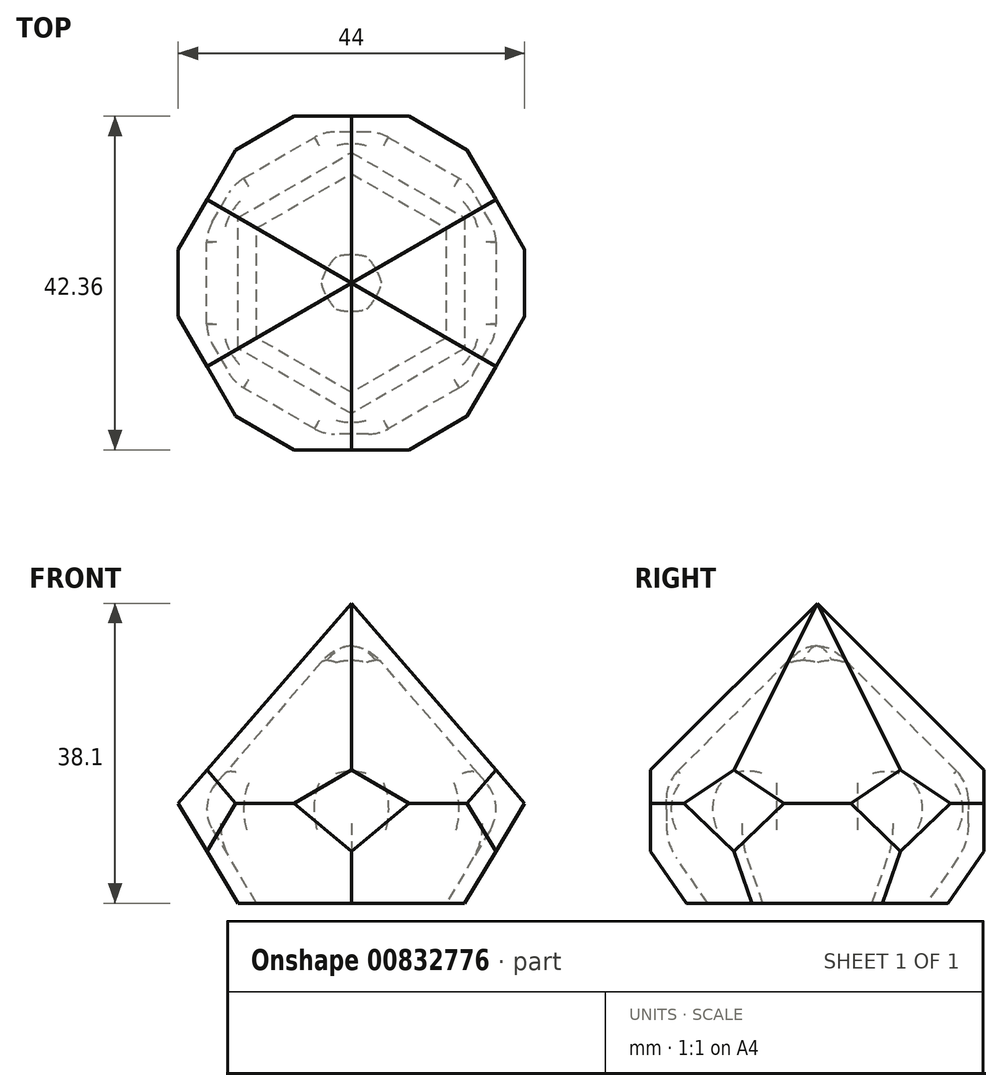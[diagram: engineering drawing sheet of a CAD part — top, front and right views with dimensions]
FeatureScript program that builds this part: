
annotation { "Feature Type Name" : "Feature", "Feature Type Description" : "" }
export const myFeature = defineFeature(function(context is Context, id is Id, definition is map)
    precondition{}
    {
        {
            var Q0;
            Q0=qCreatedBy(makeId("Top.planeOp"),FACE);
            var sketch = newSketch(context, id + "F0", { "sketchPlane" : qUnion([Q0])});
            skCircle(sketch, "E0.cCircle", {"center": v(0, 0) * mm, "radius": 25.4 * mm, "construction": true});
            skLineSegment(sketch, "E0.0", {"start": v(0, 25.4) * mm, "end": v(22, 12.7) * mm});
            skLineSegment(sketch, "E0.1", {"start": v(22, 12.7) * mm, "end": v(22, -12.7) * mm});
            skLineSegment(sketch, "E0.2", {"start": v(22, -12.7) * mm, "end": v(0, -25.4) * mm});
            skLineSegment(sketch, "E0.3", {"start": v(0, -25.4) * mm, "end": v(-22, -12.7) * mm});
            skLineSegment(sketch, "E0.4", {"start": v(-22, -12.7) * mm, "end": v(-22, 12.7) * mm});
            skLineSegment(sketch, "E0.5", {"start": v(-22, 12.7) * mm, "end": v(0, 25.4) * mm});
            skLineSegment(sketch, "E1", {"start": v(0, 0) * mm, "end": v(22, 0) * mm, "construction": true});
            skSolve(sketch);
        }
        {
            var Q0;
            Q0=makeQuery(id+"F0.imprint","IMPRINT",FACE,{"disambiguationData":[TD([[makeQuery(id+"F0.imprint","IMPRINT",EDGE,{"derivedFrom":sQuery(id+"F0.wireOp",EDGE,"E0.0")}),-1.0]])]});
            extrude(context, id + "F1", {"entities" : qUnion([Q0]), "depth" : 12.7 * mm, "offsetDistance" : 25.4 * mm});
        }
        {
            var Q0;
            Q0=makeQuery(id+"F1.opExtrude","CAP_EDGE",EDGE,{"disambiguationData":[OSD([sQuery(id+"F0.wireOp",EDGE,"E0.3")])],"isStart":true});
            var Q1;
            Q1=makeQuery(id+"F1.opExtrude","CAP_EDGE",EDGE,{"disambiguationData":[OSD([sQuery(id+"F0.wireOp",EDGE,"E0.2")])],"isStart":true});
            var Q2;
            Q2=makeQuery(id+"F1.opExtrude","CAP_FACE",FACE,{"disambiguationData":[OSD([sQuery(id+"F0.wireOp",EDGE,"E0.0"),sQuery(id+"F0.wireOp",EDGE,"E0.1"),sQuery(id+"F0.wireOp",EDGE,"E0.2"),sQuery(id+"F0.wireOp",EDGE,"E0.3"),sQuery(id+"F0.wireOp",EDGE,"E0.4"),sQuery(id+"F0.wireOp",EDGE,"E0.5")])],"isStart":true});
            chamfer(context, id + "F2", {"entities" : qUnion([Q0, Q1, Q2]), "chamferType" : ChamferType.TWO_OFFSETS, "width1" : 7.62 * mm, "oppositeDirection" : false, "width2" : 12.7 * mm, "tangentPropagation" : true});
        }
        {
            var Q0;
            Q0=makeQuery(id+"F1.opExtrude","CAP_FACE",FACE,{"disambiguationData":[OSD([sQuery(id+"F0.wireOp",EDGE,"E0.0"),sQuery(id+"F0.wireOp",EDGE,"E0.1"),sQuery(id+"F0.wireOp",EDGE,"E0.2"),sQuery(id+"F0.wireOp",EDGE,"E0.3"),sQuery(id+"F0.wireOp",EDGE,"E0.4"),sQuery(id+"F0.wireOp",EDGE,"E0.5")])],"isStart":false});
            extrude(context, id + "F3", {"entities" : qUnion([Q0]), "operationType" : NewBodyOperationType.ADD, "depth" : 25.4 * mm, "offsetDistance" : 25.4 * mm});
        }
        {
            var Q0;
            Q0=makeQuery(id+"F3.opExtrude","CAP_FACE",FACE,{"disambiguationData":[OSD([sQuery(id+"F0.wireOp",EDGE,"E0.0"),sQuery(id+"F0.wireOp",EDGE,"E0.1"),sQuery(id+"F0.wireOp",EDGE,"E0.2"),sQuery(id+"F0.wireOp",EDGE,"E0.3"),sQuery(id+"F0.wireOp",EDGE,"E0.4"),sQuery(id+"F0.wireOp",EDGE,"E0.5")])],"isStart":false});
            chamfer(context, id + "F4", {"entities" : qUnion([Q0]), "chamferType" : ChamferType.TWO_OFFSETS, "width1" : 25.4 * mm, "oppositeDirection" : false, "width2" : 22 * mm, "tangentPropagation" : true});
        }
        {
            var Q0;
            Q0=qCreatedBy(makeId("Top.planeOp"),FACE);
            var sketch = newSketch(context, id + "F5", { "sketchPlane" : qUnion([Q0])});
            skPoint(sketch, "E2.middle", {"position": v(0, 0) * mm});
            skLineSegment(sketch, "E3.bottom", {"start": v(0, -21.18) * mm, "end": v(7.62, -21.18) * mm});
            skLineSegment(sketch, "E3.top", {"start": v(0, -41.27) * mm, "end": v(7.62, -41.27) * mm});
            skLineSegment(sketch, "E3.left", {"start": v(0, -21.18) * mm, "end": v(0, -41.27) * mm});
            skLineSegment(sketch, "E3.right", {"start": v(7.62, -21.18) * mm, "end": v(7.62, -41.27) * mm});
            skLineSegment(sketch, "E4", {"start": v(0, -21.18) * mm, "end": v(-7.62, -21.18) * mm});
            skLineSegment(sketch, "E5", {"start": v(-7.62, -21.18) * mm, "end": v(-7.62, -41.27) * mm});
            skLineSegment(sketch, "E6", {"start": v(-7.62, -41.27) * mm, "end": v(0, -41.27) * mm});
            skLineSegment(sketch, "E7.1.0", {"start": v(14.53, -17.2) * mm, "end": v(31.93, -27.23) * mm});
            skLineSegment(sketch, "E7.1.1", {"start": v(18.34, -10.6) * mm, "end": v(35.74, -20.64) * mm});
            skLineSegment(sketch, "E7.1.2", {"start": v(22.15, -4) * mm, "end": v(39.55, -14.04) * mm});
            skLineSegment(sketch, "E7.1.3", {"start": v(18.34, -10.6) * mm, "end": v(22.15, -4) * mm});
            skLineSegment(sketch, "E7.1.4", {"start": v(18.34, -10.6) * mm, "end": v(14.53, -17.2) * mm});
            skLineSegment(sketch, "E7.1.5", {"start": v(31.93, -27.23) * mm, "end": v(35.74, -20.64) * mm});
            skLineSegment(sketch, "E7.1.6", {"start": v(35.74, -20.64) * mm, "end": v(39.55, -14.04) * mm});
            skLineSegment(sketch, "E7.2.0", {"start": v(22.15, 4) * mm, "end": v(39.55, 14.04) * mm});
            skLineSegment(sketch, "E7.2.1", {"start": v(18.34, 10.6) * mm, "end": v(35.74, 20.64) * mm});
            skLineSegment(sketch, "E7.2.2", {"start": v(14.53, 17.2) * mm, "end": v(31.93, 27.23) * mm});
            skLineSegment(sketch, "E7.2.3", {"start": v(18.34, 10.6) * mm, "end": v(14.53, 17.2) * mm});
            skLineSegment(sketch, "E7.2.4", {"start": v(18.34, 10.6) * mm, "end": v(22.15, 4) * mm});
            skLineSegment(sketch, "E7.2.5", {"start": v(39.55, 14.04) * mm, "end": v(35.74, 20.64) * mm});
            skLineSegment(sketch, "E7.2.6", {"start": v(35.74, 20.64) * mm, "end": v(31.93, 27.23) * mm});
            skLineSegment(sketch, "E7.3.0", {"start": v(7.62, 21.18) * mm, "end": v(7.62, 41.27) * mm});
            skLineSegment(sketch, "E7.3.1", {"start": v(0, 21.18) * mm, "end": v(0, 41.27) * mm});
            skLineSegment(sketch, "E7.3.2", {"start": v(-7.62, 21.18) * mm, "end": v(-7.62, 41.27) * mm});
            skLineSegment(sketch, "E7.3.3", {"start": v(0, 21.18) * mm, "end": v(-7.62, 21.18) * mm});
            skLineSegment(sketch, "E7.3.4", {"start": v(0, 21.18) * mm, "end": v(7.62, 21.18) * mm});
            skLineSegment(sketch, "E7.3.5", {"start": v(7.62, 41.27) * mm, "end": v(0, 41.27) * mm});
            skLineSegment(sketch, "E7.3.6", {"start": v(0, 41.27) * mm, "end": v(-7.62, 41.27) * mm});
            skLineSegment(sketch, "E7.4.0", {"start": v(-14.53, 17.2) * mm, "end": v(-31.93, 27.23) * mm});
            skLineSegment(sketch, "E7.4.1", {"start": v(-18.34, 10.6) * mm, "end": v(-35.74, 20.64) * mm});
            skLineSegment(sketch, "E7.4.2", {"start": v(-22.15, 4) * mm, "end": v(-39.55, 14.04) * mm});
            skLineSegment(sketch, "E7.4.3", {"start": v(-18.34, 10.6) * mm, "end": v(-22.15, 4) * mm});
            skLineSegment(sketch, "E7.4.4", {"start": v(-18.34, 10.6) * mm, "end": v(-14.53, 17.2) * mm});
            skLineSegment(sketch, "E7.4.5", {"start": v(-31.93, 27.23) * mm, "end": v(-35.74, 20.64) * mm});
            skLineSegment(sketch, "E7.4.6", {"start": v(-35.74, 20.64) * mm, "end": v(-39.55, 14.04) * mm});
            skLineSegment(sketch, "E7.5.0", {"start": v(-22.15, -4) * mm, "end": v(-39.55, -14.04) * mm});
            skLineSegment(sketch, "E7.5.1", {"start": v(-18.34, -10.6) * mm, "end": v(-35.74, -20.64) * mm});
            skLineSegment(sketch, "E7.5.2", {"start": v(-14.53, -17.2) * mm, "end": v(-31.93, -27.23) * mm});
            skLineSegment(sketch, "E7.5.3", {"start": v(-18.34, -10.6) * mm, "end": v(-14.53, -17.2) * mm});
            skLineSegment(sketch, "E7.5.4", {"start": v(-18.34, -10.6) * mm, "end": v(-22.15, -4) * mm});
            skLineSegment(sketch, "E7.5.5", {"start": v(-39.55, -14.04) * mm, "end": v(-35.74, -20.64) * mm});
            skLineSegment(sketch, "E7.5.6", {"start": v(-35.74, -20.64) * mm, "end": v(-31.93, -27.23) * mm});
            skSolve(sketch);
        }
        {
            var Q0;
            Q0=makeQuery(id+"F5.imprint","IMPRINT",FACE,{"disambiguationData":[TD([[makeQuery(id+"F5.imprint","IMPRINT",EDGE,{"derivedFrom":sQuery(id+"F5.wireOp",EDGE,"E3.left")}),-1.0]])]});
            var Q1;
            Q1=makeQuery(id+"F5.imprint","IMPRINT",FACE,{"disambiguationData":[TD([[makeQuery(id+"F5.imprint","IMPRINT",EDGE,{"derivedFrom":sQuery(id+"F5.wireOp",EDGE,"E3.bottom")}),-1.0]])]});
            var Q2;
            Q2=makeQuery(id+"F5.imprint","IMPRINT",FACE,{"disambiguationData":[TD([[makeQuery(id+"F5.imprint","IMPRINT",EDGE,{"derivedFrom":sQuery(id+"F5.wireOp",EDGE,"E7.5.1")}),1.0]])]});
            var Q3;
            Q3=makeQuery(id+"F5.imprint","IMPRINT",FACE,{"disambiguationData":[TD([[makeQuery(id+"F5.imprint","IMPRINT",EDGE,{"derivedFrom":sQuery(id+"F5.wireOp",EDGE,"E7.5.0")}),1.0]])]});
            var Q4;
            Q4=makeQuery(id+"F5.imprint","IMPRINT",FACE,{"disambiguationData":[TD([[makeQuery(id+"F5.imprint","IMPRINT",EDGE,{"derivedFrom":sQuery(id+"F5.wireOp",EDGE,"E7.1.1")}),1.0]])]});
            var Q5;
            Q5=makeQuery(id+"F5.imprint","IMPRINT",FACE,{"disambiguationData":[TD([[makeQuery(id+"F5.imprint","IMPRINT",EDGE,{"derivedFrom":sQuery(id+"F5.wireOp",EDGE,"E7.1.0")}),1.0]])]});
            var Q6;
            Q6=makeQuery(id+"F5.imprint","IMPRINT",FACE,{"disambiguationData":[TD([[makeQuery(id+"F5.imprint","IMPRINT",EDGE,{"derivedFrom":sQuery(id+"F5.wireOp",EDGE,"E7.3.1")}),1.0]])]});
            var Q7;
            Q7=makeQuery(id+"F5.imprint","IMPRINT",FACE,{"disambiguationData":[TD([[makeQuery(id+"F5.imprint","IMPRINT",EDGE,{"derivedFrom":sQuery(id+"F5.wireOp",EDGE,"E7.3.0")}),1.0]])]});
            var Q8;
            Q8=makeQuery(id+"F5.imprint","IMPRINT",FACE,{"disambiguationData":[TD([[makeQuery(id+"F5.imprint","IMPRINT",EDGE,{"derivedFrom":sQuery(id+"F5.wireOp",EDGE,"E7.2.1")}),1.0]])]});
            var Q9;
            Q9=makeQuery(id+"F5.imprint","IMPRINT",FACE,{"disambiguationData":[TD([[makeQuery(id+"F5.imprint","IMPRINT",EDGE,{"derivedFrom":sQuery(id+"F5.wireOp",EDGE,"E7.2.0")}),1.0]])]});
            var Q10;
            Q10=makeQuery(id+"F5.imprint","IMPRINT",FACE,{"disambiguationData":[TD([[makeQuery(id+"F5.imprint","IMPRINT",EDGE,{"derivedFrom":sQuery(id+"F5.wireOp",EDGE,"E7.4.0")}),1.0]])]});
            var Q11;
            Q11=makeQuery(id+"F5.imprint","IMPRINT",FACE,{"disambiguationData":[TD([[makeQuery(id+"F5.imprint","IMPRINT",EDGE,{"derivedFrom":sQuery(id+"F5.wireOp",EDGE,"E7.4.1")}),1.0]])]});
            extrude(context, id + "F6", {"entities" : qUnion([Q0, Q1, Q2, Q3, Q4, Q5, Q6, Q7, Q8, Q9, Q10, Q11]), "depth" : 25.4 * mm, "offsetDistance" : 25.4 * mm});
        }
        {
            var Q0;
            Q0=makeQuery(id+"F6.opExtrude","SWEPT_BODY",BODY,{"disambiguationData":[OSD([sQuery(id+"F5.wireOp",EDGE,"E3.bottom"),sQuery(id+"F5.wireOp",EDGE,"E3.top"),sQuery(id+"F5.wireOp",EDGE,"E3.right"),sQuery(id+"F5.wireOp",EDGE,"E4"),sQuery(id+"F5.wireOp",EDGE,"E5"),sQuery(id+"F5.wireOp",EDGE,"E6")])]});
            var Q1;
            Q1=makeQuery(id+"F6.opExtrude","SWEPT_BODY",BODY,{"disambiguationData":[OSD([sQuery(id+"F5.wireOp",EDGE,"E7.1.0"),sQuery(id+"F5.wireOp",EDGE,"E7.1.2"),sQuery(id+"F5.wireOp",EDGE,"E7.1.3"),sQuery(id+"F5.wireOp",EDGE,"E7.1.4"),sQuery(id+"F5.wireOp",EDGE,"E7.1.5"),sQuery(id+"F5.wireOp",EDGE,"E7.1.6")])]});
            var Q2;
            Q2=makeQuery(id+"F6.opExtrude","SWEPT_BODY",BODY,{"disambiguationData":[OSD([sQuery(id+"F5.wireOp",EDGE,"E7.5.0"),sQuery(id+"F5.wireOp",EDGE,"E7.5.2"),sQuery(id+"F5.wireOp",EDGE,"E7.5.3"),sQuery(id+"F5.wireOp",EDGE,"E7.5.4"),sQuery(id+"F5.wireOp",EDGE,"E7.5.5"),sQuery(id+"F5.wireOp",EDGE,"E7.5.6")])]});
            var Q3;
            Q3=makeQuery(id+"F6.opExtrude","SWEPT_BODY",BODY,{"disambiguationData":[OSD([sQuery(id+"F5.wireOp",EDGE,"E7.4.0"),sQuery(id+"F5.wireOp",EDGE,"E7.4.2"),sQuery(id+"F5.wireOp",EDGE,"E7.4.3"),sQuery(id+"F5.wireOp",EDGE,"E7.4.4"),sQuery(id+"F5.wireOp",EDGE,"E7.4.5"),sQuery(id+"F5.wireOp",EDGE,"E7.4.6")])]});
            var Q4;
            Q4=makeQuery(id+"F6.opExtrude","SWEPT_BODY",BODY,{"disambiguationData":[OSD([sQuery(id+"F5.wireOp",EDGE,"E7.3.0"),sQuery(id+"F5.wireOp",EDGE,"E7.3.2"),sQuery(id+"F5.wireOp",EDGE,"E7.3.3"),sQuery(id+"F5.wireOp",EDGE,"E7.3.4"),sQuery(id+"F5.wireOp",EDGE,"E7.3.5"),sQuery(id+"F5.wireOp",EDGE,"E7.3.6")])]});
            var Q5;
            Q5=makeQuery(id+"F6.opExtrude","SWEPT_BODY",BODY,{"disambiguationData":[OSD([sQuery(id+"F5.wireOp",EDGE,"E7.2.0"),sQuery(id+"F5.wireOp",EDGE,"E7.2.2"),sQuery(id+"F5.wireOp",EDGE,"E7.2.3"),sQuery(id+"F5.wireOp",EDGE,"E7.2.4"),sQuery(id+"F5.wireOp",EDGE,"E7.2.5"),sQuery(id+"F5.wireOp",EDGE,"E7.2.6")])]});
            var Q6;
            Q6=makeQuery(id+"F1.opExtrude","SWEPT_BODY",BODY,{"disambiguationData":[OSD([sQuery(id+"F0.wireOp",EDGE,"E0.0"),sQuery(id+"F0.wireOp",EDGE,"E0.1"),sQuery(id+"F0.wireOp",EDGE,"E0.2"),sQuery(id+"F0.wireOp",EDGE,"E0.3"),sQuery(id+"F0.wireOp",EDGE,"E0.4"),sQuery(id+"F0.wireOp",EDGE,"E0.5")])]});
            booleanBodies(context, id + "F7", {"operationType" : BooleanOperationType.SUBTRACTION, "tools" : qUnion([Q0, Q1, Q2, Q3, Q4, Q5]), "targets" : qUnion([Q6])});
        }
        {
            var Q0;
            Q0=makeQuery(id+"F1.opExtrude","CAP_FACE",FACE,{"disambiguationData":[OSD([sQuery(id+"F0.wireOp",EDGE,"E0.0"),sQuery(id+"F0.wireOp",EDGE,"E0.1"),sQuery(id+"F0.wireOp",EDGE,"E0.2"),sQuery(id+"F0.wireOp",EDGE,"E0.3"),sQuery(id+"F0.wireOp",EDGE,"E0.4"),sQuery(id+"F0.wireOp",EDGE,"E0.5")])],"isStart":true});
            shell(context, id + "F8", {"entities" : qUnion([Q0]), "thickness" : 2 * mm});
        }
        {
            var Q0;
            {var subQ0=sQuery(id+"F0.wireOp",EDGE,"E0.5");var subQ1=sQuery(id+"F0.wireOp",EDGE,"E0.4");var subQ2=sQuery(id+"F0.wireOp",EDGE,"E0.3");var subQ3=sQuery(id+"F0.wireOp",EDGE,"E0.2");var subQ4=sQuery(id+"F0.wireOp",EDGE,"E0.1");var subQ5=sQuery(id+"F0.wireOp",EDGE,"E0.0");Q0=makeQuery(id+"F8.opShell","OFFSET_FACE",FACE,{"disambiguationData":[OSD([subQ5,subQ4,subQ3,subQ2,subQ1,subQ0]),TDD([makeQuery(id+"F4.opChamfer","BLEND_FACE",FACE,{"disambiguationData":[OSD([subQ5,subQ4,subQ3,subQ2,subQ1,subQ0]),TDD([makeQuery(id+"F3.opExtrude","CAP_EDGE",EDGE,{"disambiguationData":[OSD([subQ5,subQ4,subQ3,subQ2,subQ1,subQ0]),TDD([makeQuery(id+"F2.opChamfer","BLEND_EDGE",EDGE,{"blendedFrom":[makeQuery(id+"F1.opExtrude","CAP_EDGE",EDGE,{"disambiguationData":[OSD([subQ3])],"isStart":true}),makeQuery(id+"F1.opExtrude","CAP_FACE",FACE,{"disambiguationData":[OSD([subQ5,subQ4,subQ3,subQ2,subQ1,subQ0])],"isStart":false})],"blendedInto":[makeQuery(id+"F1.opExtrude","CAP_FACE",FACE,{"disambiguationData":[OSD([subQ5,subQ4,subQ3,subQ2,subQ1,subQ0])],"isStart":false})]})])],"isStart":false})])]})])]});}
            var Q1;
            {var subQ0=sQuery(id+"F0.wireOp",EDGE,"E0.5");var subQ1=sQuery(id+"F0.wireOp",EDGE,"E0.4");var subQ2=sQuery(id+"F0.wireOp",EDGE,"E0.3");var subQ3=sQuery(id+"F0.wireOp",EDGE,"E0.2");var subQ4=sQuery(id+"F0.wireOp",EDGE,"E0.1");var subQ5=sQuery(id+"F0.wireOp",EDGE,"E0.0");Q1=makeQuery(id+"F8.opShell","OFFSET_FACE",FACE,{"disambiguationData":[OSD([subQ5,subQ4,subQ3,subQ2,subQ1,subQ0]),TDD([makeQuery(id+"F4.opChamfer","BLEND_FACE",FACE,{"disambiguationData":[OSD([subQ5,subQ4,subQ3,subQ2,subQ1,subQ0]),TDD([makeQuery(id+"F3.opExtrude","CAP_EDGE",EDGE,{"disambiguationData":[OSD([subQ5,subQ4,subQ3,subQ2,subQ1,subQ0]),TDD([makeQuery(id+"F2.opChamfer","BLEND_EDGE",EDGE,{"blendedFrom":[makeQuery(id+"F1.opExtrude","CAP_EDGE",EDGE,{"disambiguationData":[OSD([subQ4])],"isStart":true}),makeQuery(id+"F1.opExtrude","CAP_FACE",FACE,{"disambiguationData":[OSD([subQ5,subQ4,subQ3,subQ2,subQ1,subQ0])],"isStart":false})],"blendedInto":[makeQuery(id+"F1.opExtrude","CAP_FACE",FACE,{"disambiguationData":[OSD([subQ5,subQ4,subQ3,subQ2,subQ1,subQ0])],"isStart":false})]})])],"isStart":false})])]})])]});}
            var Q2;
            {var subQ0=sQuery(id+"F0.wireOp",EDGE,"E0.5");var subQ1=sQuery(id+"F0.wireOp",EDGE,"E0.4");var subQ2=sQuery(id+"F0.wireOp",EDGE,"E0.3");var subQ3=sQuery(id+"F0.wireOp",EDGE,"E0.2");var subQ4=sQuery(id+"F0.wireOp",EDGE,"E0.1");var subQ5=sQuery(id+"F0.wireOp",EDGE,"E0.0");Q2=makeQuery(id+"F8.opShell","OFFSET_FACE",FACE,{"disambiguationData":[OSD([subQ5,subQ4,subQ3,subQ2,subQ1,subQ0]),TDD([makeQuery(id+"F4.opChamfer","BLEND_FACE",FACE,{"disambiguationData":[OSD([subQ5,subQ4,subQ3,subQ2,subQ1,subQ0]),TDD([makeQuery(id+"F3.opExtrude","CAP_EDGE",EDGE,{"disambiguationData":[OSD([subQ5,subQ4,subQ3,subQ2,subQ1,subQ0]),TDD([makeQuery(id+"F2.opChamfer","BLEND_EDGE",EDGE,{"blendedFrom":[makeQuery(id+"F1.opExtrude","CAP_EDGE",EDGE,{"disambiguationData":[OSD([subQ2])],"isStart":true}),makeQuery(id+"F1.opExtrude","CAP_FACE",FACE,{"disambiguationData":[OSD([subQ5,subQ4,subQ3,subQ2,subQ1,subQ0])],"isStart":false})],"blendedInto":[makeQuery(id+"F1.opExtrude","CAP_FACE",FACE,{"disambiguationData":[OSD([subQ5,subQ4,subQ3,subQ2,subQ1,subQ0])],"isStart":false})]})])],"isStart":false})])]})])]});}
            var Q3;
            {var subQ0=sQuery(id+"F0.wireOp",EDGE,"E0.5");var subQ1=sQuery(id+"F0.wireOp",EDGE,"E0.4");var subQ2=sQuery(id+"F0.wireOp",EDGE,"E0.3");var subQ3=sQuery(id+"F0.wireOp",EDGE,"E0.2");var subQ4=sQuery(id+"F0.wireOp",EDGE,"E0.1");var subQ5=sQuery(id+"F0.wireOp",EDGE,"E0.0");Q3=makeQuery(id+"F8.opShell","OFFSET_FACE",FACE,{"disambiguationData":[OSD([subQ5,subQ4,subQ3,subQ2,subQ1,subQ0]),TDD([makeQuery(id+"F4.opChamfer","BLEND_FACE",FACE,{"disambiguationData":[OSD([subQ5,subQ4,subQ3,subQ2,subQ1,subQ0]),TDD([makeQuery(id+"F3.opExtrude","CAP_EDGE",EDGE,{"disambiguationData":[OSD([subQ5,subQ4,subQ3,subQ2,subQ1,subQ0]),TDD([makeQuery(id+"F2.opChamfer","BLEND_EDGE",EDGE,{"blendedFrom":[makeQuery(id+"F1.opExtrude","CAP_EDGE",EDGE,{"disambiguationData":[OSD([subQ1])],"isStart":true}),makeQuery(id+"F1.opExtrude","CAP_FACE",FACE,{"disambiguationData":[OSD([subQ5,subQ4,subQ3,subQ2,subQ1,subQ0])],"isStart":false})],"blendedInto":[makeQuery(id+"F1.opExtrude","CAP_FACE",FACE,{"disambiguationData":[OSD([subQ5,subQ4,subQ3,subQ2,subQ1,subQ0])],"isStart":false})]})])],"isStart":false})])]})])]});}
            var Q4;
            {var subQ0=sQuery(id+"F0.wireOp",EDGE,"E0.5");var subQ1=sQuery(id+"F0.wireOp",EDGE,"E0.4");var subQ2=sQuery(id+"F0.wireOp",EDGE,"E0.3");var subQ3=sQuery(id+"F0.wireOp",EDGE,"E0.2");var subQ4=sQuery(id+"F0.wireOp",EDGE,"E0.1");var subQ5=sQuery(id+"F0.wireOp",EDGE,"E0.0");Q4=makeQuery(id+"F8.opShell","OFFSET_FACE",FACE,{"disambiguationData":[OSD([subQ5,subQ4,subQ3,subQ2,subQ1,subQ0]),TDD([makeQuery(id+"F4.opChamfer","BLEND_FACE",FACE,{"disambiguationData":[OSD([subQ5,subQ4,subQ3,subQ2,subQ1,subQ0]),TDD([makeQuery(id+"F3.opExtrude","CAP_EDGE",EDGE,{"disambiguationData":[OSD([subQ5,subQ4,subQ3,subQ2,subQ1,subQ0]),TDD([makeQuery(id+"F2.opChamfer","BLEND_EDGE",EDGE,{"blendedFrom":[makeQuery(id+"F1.opExtrude","CAP_EDGE",EDGE,{"disambiguationData":[OSD([subQ0])],"isStart":true}),makeQuery(id+"F1.opExtrude","CAP_FACE",FACE,{"disambiguationData":[OSD([subQ5,subQ4,subQ3,subQ2,subQ1,subQ0])],"isStart":false})],"blendedInto":[makeQuery(id+"F1.opExtrude","CAP_FACE",FACE,{"disambiguationData":[OSD([subQ5,subQ4,subQ3,subQ2,subQ1,subQ0])],"isStart":false})]})])],"isStart":false})])]})])]});}
            var Q5;
            {var subQ0=sQuery(id+"F0.wireOp",EDGE,"E0.5");var subQ1=sQuery(id+"F0.wireOp",EDGE,"E0.4");var subQ2=sQuery(id+"F0.wireOp",EDGE,"E0.3");var subQ3=sQuery(id+"F0.wireOp",EDGE,"E0.2");var subQ4=sQuery(id+"F0.wireOp",EDGE,"E0.1");var subQ5=sQuery(id+"F0.wireOp",EDGE,"E0.0");Q5=makeQuery(id+"F8.opShell","OFFSET_FACE",FACE,{"disambiguationData":[OSD([subQ5,subQ4,subQ3,subQ2,subQ1,subQ0]),TDD([makeQuery(id+"F4.opChamfer","BLEND_FACE",FACE,{"disambiguationData":[OSD([subQ5,subQ4,subQ3,subQ2,subQ1,subQ0]),TDD([makeQuery(id+"F3.opExtrude","CAP_EDGE",EDGE,{"disambiguationData":[OSD([subQ5,subQ4,subQ3,subQ2,subQ1,subQ0]),TDD([makeQuery(id+"F2.opChamfer","BLEND_EDGE",EDGE,{"blendedFrom":[makeQuery(id+"F1.opExtrude","CAP_EDGE",EDGE,{"disambiguationData":[OSD([subQ5])],"isStart":true}),makeQuery(id+"F1.opExtrude","CAP_FACE",FACE,{"disambiguationData":[OSD([subQ5,subQ4,subQ3,subQ2,subQ1,subQ0])],"isStart":false})],"blendedInto":[makeQuery(id+"F1.opExtrude","CAP_FACE",FACE,{"disambiguationData":[OSD([subQ5,subQ4,subQ3,subQ2,subQ1,subQ0])],"isStart":false})]})])],"isStart":false})])]})])]});}
            var Q6;
            Q6=makeQuery(id+"F8.opShell","OFFSET_EDGE",EDGE,{"disambiguationData":[OSD([sQuery(id+"F0.wireOp",EDGE,"E0.3"),sQuery(id+"F5.wireOp",EDGE,"E3.bottom"),sQuery(id+"F5.wireOp",EDGE,"E4")])]});
            var Q7;
            Q7=makeQuery(id+"F8.opShell","OFFSET_EDGE",EDGE,{"disambiguationData":[OSD([sQuery(id+"F0.wireOp",EDGE,"E0.2"),sQuery(id+"F5.wireOp",EDGE,"E3.bottom"),sQuery(id+"F5.wireOp",EDGE,"E4")])]});
            var Q8;
            Q8=makeQuery(id+"F8.opShell","OFFSET_FACE",FACE,{"disambiguationData":[OSD([sQuery(id+"F5.wireOp",EDGE,"E7.5.3"),sQuery(id+"F5.wireOp",EDGE,"E7.5.4")])]});
            var Q9;
            Q9=makeQuery(id+"F8.opShell","OFFSET_FACE",FACE,{"disambiguationData":[OSD([sQuery(id+"F5.wireOp",EDGE,"E7.4.3"),sQuery(id+"F5.wireOp",EDGE,"E7.4.4")])]});
            var Q10;
            Q10=makeQuery(id+"F8.opShell","OFFSET_FACE",FACE,{"disambiguationData":[OSD([sQuery(id+"F5.wireOp",EDGE,"E7.1.3"),sQuery(id+"F5.wireOp",EDGE,"E7.1.4")])]});
            var Q11;
            Q11=makeQuery(id+"F8.opShell","OFFSET_FACE",FACE,{"disambiguationData":[OSD([sQuery(id+"F5.wireOp",EDGE,"E7.2.3"),sQuery(id+"F5.wireOp",EDGE,"E7.2.4")])]});
            var Q12;
            Q12=makeQuery(id+"F8.opShell","OFFSET_FACE",FACE,{"disambiguationData":[OSD([sQuery(id+"F5.wireOp",EDGE,"E7.3.3"),sQuery(id+"F5.wireOp",EDGE,"E7.3.4")])]});
            fillet(context, id + "F9", {"entities" : qUnion([Q0, Q1, Q2, Q3, Q4, Q5, Q6, Q7, Q8, Q9, Q10, Q11, Q12]), "radius" : 5.08 * mm, "tangentPropagation" : true, "allowEdgeOverflow" : false});
        }
    });
